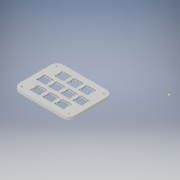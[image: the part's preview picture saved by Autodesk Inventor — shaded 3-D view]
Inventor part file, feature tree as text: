
AUTODESK INVENTOR PART (.ipt)
format: ipt  version: 2019 (Build 230136000, 136)  size: 909,824 bytes
history: native  units: in
note: dims shown in document units (in); Inventor stores cm internally (conversion verified against a paired STEP export)
features: sketch x4, extrude x2, fillet x1, hole x1
ambient origin geometry x8: Origin, YZ Plane, XZ Plane, XY Plane, X Axis, Y Axis, Z Axis, Center Point
bodies: Solid1 (feature_tree)
feature tree (8):
  sketch  "Sketch1"  dims[d0=90.0deg d1=90.0deg d2=90.0deg]
  extrude  "Extrusion1"  TaperAngle=90.0deg  [1 undecoded]
  fillet  "Fillet2"  [1 undecoded]
  hole  "Hole1"  [1 undecoded]
  extrude  "Extrusion4"  TaperAngle=90.0deg  [1 undecoded]
  sketch  "Sketch2"  dims[d3=90.0deg d4=90.0deg]
  sketch  "Sketch5"  dims[d5=90.0deg d6=90.0deg]
  sketch  "Sketch6"  dims[d7=90.0deg d8=90.0deg d9=90.0deg d10=90.0deg d11=90.0deg d12=90.0deg d13=90.0deg d14=90.0deg d15=90.0deg d16=90.0deg d17=90.0deg d18=90.0deg d19=90.0deg d20=90.0deg d21=90.0deg d22=90.0deg d23=90.0deg d24=90.0deg d25=90.0deg d26=90.0deg d27=90.0deg d28=90.0deg d29=90.0deg d30=90.0deg d31=90.0deg d32=90.0deg d33=90.0deg d34=90.0deg d35=90.0deg d36=90.0deg d37=90.0deg d38=90.0deg d39=90.0deg d40=90.0deg d41=90.0deg d42=90.0deg d43=90.0deg d44=90.0deg d45=90.0deg d46=90.0deg d47=90.0deg d48=90.0deg d49=90.0deg d50=90.0deg d51=90.0deg d52=90.0deg d53=90.0deg d54=90.0deg d55=90.0deg d56=90.0deg d57=90.0deg d58=90.0deg d59=90.0deg d60=90.0deg d61=90.0deg d62=90.0deg d63=90.0deg d64=90.0deg d65=90.0deg d66=90.0deg d67=90.0deg d68=90.0deg d69=90.0deg d70=90.0deg d71=90.0deg d72=90.0deg d73=90.0deg d74=90.0deg d75=90.0deg d76=90.0deg d77=90.0deg d78=90.0deg d79=90.0deg d80=90.0deg d81=90.0deg d82=90.0deg d83=90.0deg d84=90.0deg d85=90.0deg d86=90.0deg d87=90.0deg d88=90.0deg d89=90.0deg d90=90.0deg d91=90.0deg d92=90.0deg d93=90.0deg d94=90.0deg d95=90.0deg d96=90.0deg d97=90.0deg d98=90.0deg d99=90.0deg d100=90.0deg d101=90.0deg d102=90.0deg d103=90.0deg d104=90.0deg d105=90.0deg d106=90.0deg d107=90.0deg d108=90.0deg d109=90.0deg d110=90.0deg d111=90.0deg d112=90.0deg d113=90.0deg d114=90.0deg d115=90.0deg d116=90.0deg d117=90.0deg d118=90.0deg d119=90.0deg d120=90.0deg d121=90.0deg d122=90.0deg d123=90.0deg d124=90.0deg d125=90.0deg d126=90.0deg d127=90.0deg d128=90.0deg d129=90.0deg d130=90.0deg d131=90.0deg d132=90.0deg d133=90.0deg d134=90.0deg d135=90.0deg d136=90.0deg d137=90.0deg d138=90.0deg d139=90.0deg d140=90.0deg d141=90.0deg d142=90.0deg d143=90.0deg d144=90.0deg d145=90.0deg d146=90.0deg d147=90.0deg d148=90.0deg d149=90.0deg d150=90.0deg d151=90.0deg d152=90.0deg d153=90.0deg d154=0.0679in d155=0.0995in d156=0.4429in d157=0.4745in d158=0.6506in d159=0.6821in d160=0.8179in d161=0.8495in d162=1.0256in d163=1.0571in d164=1.1929in d165=1.2245in d166=1.4006in d167=1.4321in d168=1.5679in d169=1.5995in d170=1.7756in d171=1.8071in d172=1.9429in d173=1.9745in d174=2.1506in d175=2.1821in d176=2.3179in d177=2.3495in d178=2.5256in d179=2.5571in d180=2.9006in d181=2.9321in d182=3.0in d183=0.122in d184=0.3504in d185=0.4724in d186=0.0394in d187=0.5118in d188=0.75in d189=0.628in d190=0.3996in d191=0.2776in d192=0.75in d193=0.872in d194=1.1004in d195=1.2224in d196=0.7894in d197=0.2382in d198=0.7106in d199=1.2618in d200=0.8887in d201=1.3613in d202=4.9723in d203=4.9043in d204=3.3336in d205=4.8728in d206=4.8728in d207=4.5293in d208=4.5293in d209=4.5293in d210=4.4978in d211=4.4978in d212=4.4978in d213=4.4978in d214=4.4978in d215=4.3216in d216=4.3216in d217=3.3336in d218=3.2116in d219=2.9833in d220=2.8612in d221=4.2902in d222=4.1543in d223=3.3336in d224=3.2116in d225=2.9833in d226=2.8612in d227=4.1228in d228=4.1228in d229=3.9466in d230=3.9466in d231=3.9466in d232=3.9466in d233=3.9466in d234=4.0836in d235=3.9616in d236=3.7333in d237=3.6112in d238=2.5836in d239=2.4616in d240=2.2333in d241=2.1112in d242=3.9152in d243=3.9152in d244=3.9152in d245=3.373in d246=2.8219in d247=3.7793in d248=3.7793in d249=3.7793in d250=4.0836in d251=3.9616in d252=3.7333in d253=3.6112in d254=2.5836in d255=2.4616in d256=2.2333in d257=2.1112in d258=3.7478in d259=3.7478in d260=3.7478in d261=3.7478in d262=3.7478in d263=3.5716in d264=3.5716in d265=3.3336in d266=3.2116in d267=2.9833in d268=2.8612in d269=3.5402in d270=4.123in d271=3.5719in d272=2.623in d273=2.0719in d274=3.4043in d275=3.3336in d276=3.2116in d277=2.9833in d278=2.8612in d279=3.3728in d280=3.3728in d281=3.1966in d282=3.1966in d283=3.1966in d284=3.1966in d285=3.1966in d286=4.0836in d287=3.9616in d288=3.7333in d289=3.6112in d290=2.5836in d291=2.4616in d292=2.2333in d293=2.1112in d294=3.1652in d295=3.1652in d296=3.1652in d297=3.373in d298=2.8219in d299=3.0293in d300=3.0293in d301=3.0293in d302=4.0836in d303=3.9616in d304=3.7333in d305=3.6112in d306=2.5836in d307=2.4616in d308=2.2333in d309=2.1112in d310=2.9978in d311=2.9978in d312=2.9978in d313=2.9978in d314=2.9978in d315=2.8216in d316=2.8216in d317=3.3336in d318=3.2116in d319=2.9833in d320=2.8612in d321=2.7902in d322=4.123in d323=3.5719in d324=2.623in d325=2.0719in d326=2.6543in d327=3.3336in d328=3.2116in d329=2.9833in d330=2.8612in d331=2.6228in d332=2.6228in d333=2.4466in d334=2.4466in d335=2.4466in d336=2.4466in d337=2.4466in d338=4.0836in d339=3.9616in d340=3.7333in d341=3.6112in d342=2.5836in d343=2.4616in d344=2.2333in d345=2.1112in d346=2.4152in d347=2.4152in d348=2.4152in d349=3.373in d350=2.8219in d351=2.0716in d352=2.0716in d353=3.3336in d354=3.2116in d355=2.9833in d356=2.8612in d357=2.0402in d358=0.0in d359=0.8887in d360=0.0in d361=1.3613in d362=0.0679in d363=0.0in d364=0.0679in d365=0.122in d366=0.0679in d367=0.3504in d368=0.0679in d369=0.4724in d370=0.0995in d371=0.0394in d372=0.0995in d373=0.0in d374=0.0995in d375=0.122in d376=0.0995in d377=0.3504in d378=0.0995in d379=0.4724in d380=0.0995in d381=0.5118in d382=0.4429in d383=0.75in d384=0.4429in d385=0.628in d386=0.4429in d387=0.3996in d388=0.4429in d389=0.2776in d390=0.4429in d391=0.75in d392=0.4429in d393=0.872in d394=0.4429in d395=1.1004in d396=0.4429in d397=1.2224in d398=0.4745in d399=0.7894in d400=0.4745in d401=0.75in d402=0.4745in d403=0.628in d404=0.4745in d405=0.3996in d406=0.4745in d407=0.2776in d408=0.4745in d409=0.2382in d410=0.4745in d411=0.7106in d412=0.4745in d413=0.75in d414=0.4745in d415=0.872in d416=0.4745in d417=1.1004in d418=0.4745in d419=1.2224in d420=0.4745in d421=1.2618in d422=0.6506in d423=0.0394in d424=0.0in d425=0.6506in d426=0.6506in d427=0.122in d428=0.3504in d429=0.6506in d430=0.4724in d431=0.6506in d432=0.6506in d433=0.5118in d434=0.6821in d435=0.0in d436=0.122in d437=0.6821in d438=0.3504in d439=0.6821in d440=0.4724in d441=0.6821in d442=0.0in d443=0.8179in d444=0.122in d445=0.8179in d446=0.3504in d447=0.8179in d448=0.8179in d449=0.4724in d450=0.0394in d451=0.8495in d452=0.0in d453=0.8495in d454=0.122in d455=0.8495in d456=0.8495in d457=0.3504in d458=0.4724in d459=0.8495in d460=0.8495in d461=0.5118in d462=1.0256in d463=0.7894in d464=0.75in d465=1.0256in d466=1.0256in d467=0.628in d468=0.3996in d469=1.0256in d470=0.2776in d471=1.0256in d472=1.0256in d473=0.2382in d474=1.0256in d475=0.7106in d476=0.75in d477=1.0256in d478=1.0256in d479=0.872in d480=1.1004in d481=1.0256in d482=1.0256in d483=1.2224in d484=1.0256in d485=1.2618in d486=1.0571in d487=0.75in d488=0.628in d489=1.0571in d490=0.3996in d491=1.0571in d492=0.2776in d493=1.0571in d494=1.0571in d495=0.75in d496=0.872in d497=1.0571in d498=1.0571in d499=1.1004in d500=1.2224in d501=1.0571in d502=0.75in d503=1.1929in d504=0.628in d505=1.1929in d506=0.3996in d507=1.1929in d508=1.1929in d509=0.2776in d510=0.75in d511=1.1929in d512=1.1929in d513=0.872in d514=1.1004in d515=1.1929in d516=1.1929in d517=1.2224in d518=0.7894in d519=1.2245in d520=0.75in d521=1.2245in d522=0.628in d523=1.2245in d524=1.2245in d525=0.3996in d526=0.2776in d527=1.2245in d528=1.2245in d529=0.2382in d530=0.7106in d531=1.2245in d532=1.2245in d533=0.75in d534=0.872in d535=1.2245in d536=1.2245in d537=1.1004in d538=1.2224in d539=1.2245in d540=1.2245in d541=1.2618in d542=0.0394in d543=1.4006in d544=0.0in d545=1.4006in d546=1.4006in d547=0.122in d548=0.3504in d549=1.4006in d550=0.4724in d551=1.4006in d552=0.5118in d553=1.4006in d554=1.4321in d555=0.0in d556=0.122in d557=1.4321in d558=0.3504in d559=1.4321in d560=0.4724in d561=1.4321in d562=0.0in d563=1.5679in d564=0.122in d565=1.5679in d566=0.3504in d567=1.5679in d568=1.5679in d569=0.4724in d570=0.0394in d571=1.5995in d572=0.0in d573=1.5995in d574=0.122in d575=1.5995in d576=1.5995in d577=0.3504in d578=0.4724in d579=1.5995in d580=1.5995in d581=0.5118in d582=0.7894in d583=1.7756in d584=0.75in d585=1.7756in d586=1.7756in d587=0.628in d588=0.3996in d589=1.7756in d590=0.2776in d591=1.7756in d592=0.2382in d593=1.7756in d594=0.7106in d595=1.7756in d596=0.75in d597=1.7756in d598=1.7756in d599=0.872in d600=1.1004in d601=1.7756in d602=1.7756in d603=1.2224in d604=1.2618in d605=1.7756in d606=1.8071in d607=0.75in d608=0.628in d609=1.8071in d610=0.3996in d611=1.8071in d612=0.2776in d613=1.8071in d614=1.8071in d615=0.75in d616=0.872in d617=1.8071in d618=1.8071in d619=1.1004in d620=1.2224in d621=1.8071in d622=0.75in d623=1.9429in d624=0.628in d625=1.9429in d626=0.3996in d627=1.9429in d628=1.9429in d629=0.2776in d630=0.75in d631=1.9429in d632=1.9429in d633=0.872in d634=1.1004in d635=1.9429in d636=1.9429in d637=1.2224in d638=0.7894in d639=1.9745in d640=0.75in d641=1.9745in d642=0.628in d643=1.9745in d644=1.9745in d645=0.3996in d646=0.2776in d647=1.9745in d648=1.9745in d649=0.2382in d650=0.7106in d651=1.9745in d652=1.9745in d653=0.75in d654=0.872in d655=1.9745in d656=1.9745in d657=1.1004in d658=1.2224in d659=1.9745in d660=1.9745in d661=1.2618in d662=0.0394in d663=2.1506in d664=0.0in d665=2.1506in d666=2.1506in d667=0.122in d668=0.3504in d669=2.1506in d670=0.4724in d671=2.1506in d672=0.5118in d673=2.1506in d674=2.1821in d675=0.0in d676=0.122in d677=2.1821in d678=0.3504in d679=2.1821in d680=0.4724in d681=2.1821in d682=0.0in d683=2.3179in d684=0.122in d685=2.3179in d686=0.3504in d687=2.3179in d688=2.3179in d689=0.4724in d690=0.0394in d691=2.3495in d692=0.0in d693=2.3495in d694=0.122in d695=2.3495in d696=2.3495in d697=0.3504in d698=0.4724in d699=2.3495in d700=2.3495in d701=0.5118in d702=0.7894in d703=2.5256in d704=0.75in d705=2.5256in d706=2.5256in d707=0.628in d708=0.3996in d709=2.5256in d710=0.2776in d711=2.5256in d712=0.2382in d713=2.5256in d714=0.7106in d715=2.5256in d716=0.75in d717=2.5256in d718=2.5256in d719=0.872in d720=1.1004in d721=2.5256in d722=2.5256in d723=1.2224in d724=1.2618in d725=2.5256in d726=2.5571in d727=0.75in d728=0.628in d729=2.5571in d730=0.3996in d731=2.5571in d732=0.2776in d733=2.5571in d734=2.5571in d735=0.75in d736=0.872in d737=2.5571in d738=2.5571in d739=1.1004in d740=1.2224in d741=2.5571in d742=0.0394in d743=2.9006in d744=0.0in d745=2.9006in d746=2.9006in d747=0.122in d748=0.3504in d749=2.9006in d750=0.4724in d751=2.9006in d752=0.5118in d753=2.9006in d754=2.9321in d755=0.0in d756=0.122in d757=2.9321in d758=0.3504in d759=2.9321in d760=0.4724in d761=2.9321in d762=3.0in d763=0.8887in d764=3.0in d765=1.3613in d766=0.2362in d767=0.2362in d768=0.2362in d769=0.2362in d770=0.0591in d771=0.0in d789=0.3937in d790=0.2756in d791=0.2756in d792=0.2756in d793=0.2756in d794=0.2756in d795=0.2756in d796=0.2756in d797=0.2756in d798=0.1181in d799=0.1181in d800=0.1181in d801=0.1181in d802=0.1181in d803=0.2362in d804=0.1575in d805=0.0787in d806=90.0deg d807=0.315in d808=0.8108in d809=0.6299in d810=0.1181in d811=0.1181in d812=0.9252in d813=0.9311in d814=0.5512in d815=0.5512in d816=0.2756in d817=0.2756in d818=0.5512in d819=0.5512in d820=0.1575in d821=0.1575in d822=0.1181in d823=0.0in]
note: 4 required parameter values undecoded (feature->parameter linkage not recoverable at this tier; creation-order binding heuristic only, values carry confidence <= 0.55)
